# Revit family: Valve-Touchless_Hybrid-KOHLER-Wall_Mount-K-11830
name_source: partatom
category: Plumbing Fixtures
revit_build: Autodesk Revit 2015 (Build: 20140606_1530(x64)
units: mm (PartAtom-declared; Revit-internal decimal feet)

## types (1)
- NA-Not Applicable
    ADA Compliant = Yes
    Assembly Code = D2020
    CW Connection = Yes
    Cold Water Inlet = Cold Water Inlet
    Date Modified = 01/18/2019
    Default Elevation = 36"
    Description = Touchless round hybrid valve and sensor kit
    Finish = Kohler-Metal-Brass
    Flow Rate = 1 GPM
    HW Connection = No
    Height = 10"
    Hot Water Inlet = Hot Water Inlet
    Length = 3 1/8"
    Manufacturer = KOHLER Co.
    MasterFormat 1995 = 154300
    MasterFormat 2004 = 22.11.00
    Material = Brass construction
    Model = K-11830-NA
    Pressure = 45.00 psi
    Product Documentation Link = https://www.us.kohler.com
    Product Name = Wall-mount
    Product Page URL = http://www.us.kohler.com
    URL = https://www.us.kohler.com
    Vent Connection = No
    Waste Connection = No
    Waste Water Outlet = Waste Water Outlet
    Width = 9"

## geometry (parser evidence)
native form markers: Sweep x5
no freeform markers — native parametric forms only
